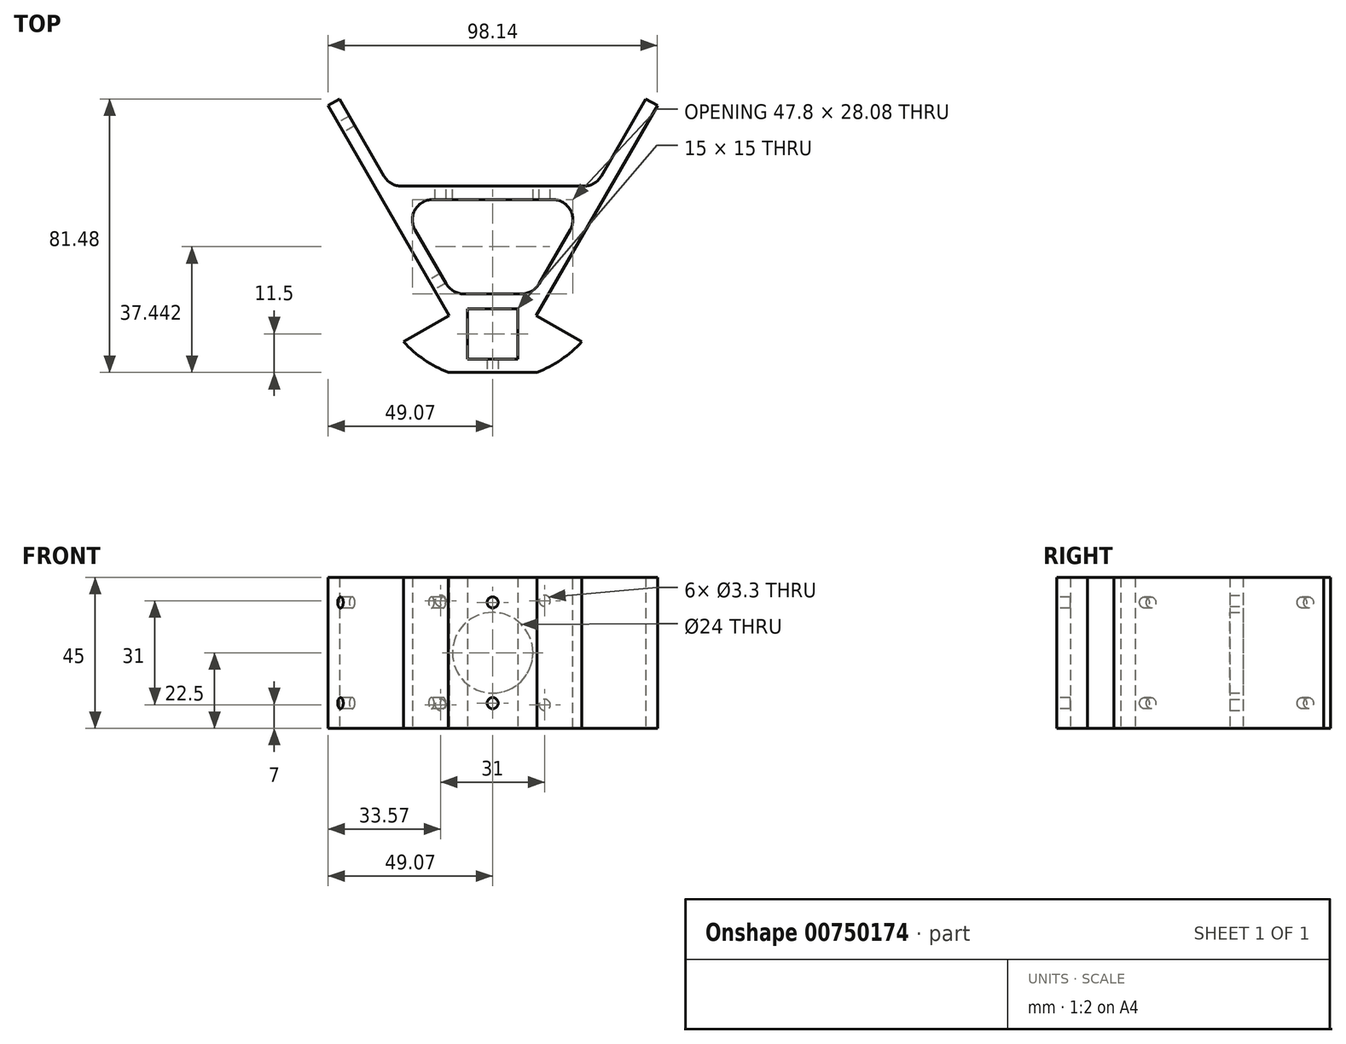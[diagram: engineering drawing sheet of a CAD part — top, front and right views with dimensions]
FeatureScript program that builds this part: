
annotation { "Feature Type Name" : "Feature", "Feature Type Description" : "" }
export const myFeature = defineFeature(function(context is Context, id is Id, definition is map)
    precondition{}
    {
        {
            var Q0;
            Q0=qCreatedBy(makeId("Top.planeOp"),FACE);
            var sketch = newSketch(context, id + "F0", { "sketchPlane" : qUnion([Q0])});
            skLineSegment(sketch, "E0.bottom", {"start": v(7.5, 7.5) * mm, "end": v(-7.5, 7.5) * mm});
            skLineSegment(sketch, "E0.top", {"start": v(7.5, -7.5) * mm, "end": v(-7.5, -7.5) * mm});
            skLineSegment(sketch, "E0.left", {"start": v(7.5, 7.5) * mm, "end": v(7.5, -7.5) * mm});
            skLineSegment(sketch, "E0.right", {"start": v(-7.5, 7.5) * mm, "end": v(-7.5, -7.5) * mm});
            skPoint(sketch, "E0.middle", {"position": v(0, 0) * mm});
            skLineSegment(sketch, "E1", {"start": v(-9.53, 7.48) * mm, "end": v(-12.08, 11.9) * mm, "construction": true});
            skLineSegment(sketch, "E2", {"start": v(-45.61, 69.98) * mm, "end": v(-49.07, 67.98) * mm});
            skLineSegment(sketch, "E3", {"start": v(-49.07, 67.98) * mm, "end": v(-13, 5.48) * mm});
            skPoint(sketch, "E4", {"position": v(0, -14.02) * mm});
            skLineSegment(sketch, "E5", {"start": v(0, -14.02) * mm, "end": v(0, 69.98) * mm, "construction": true});
            skLineSegment(sketch, "E6", {"start": v(-13, 5.48) * mm, "end": v(-26.54, -2.34) * mm});
            skLineSegment(sketch, "E7", {"start": v(-9.53, 7.48) * mm, "end": v(0, 12.98) * mm, "construction": true});
            skLineSegment(sketch, "E8", {"start": v(-13, 5.48) * mm, "end": v(-9.53, 7.48) * mm, "construction": true});
            skLineSegment(sketch, "E9", {"start": v(-8, 8.37) * mm, "end": v(-7.5, 7.5) * mm, "construction": true});
            skLineSegment(sketch, "E10", {"start": v(0, 39.98) * mm, "end": v(-28.3, 39.98) * mm});
            skArc(sketch, "E11.trimOffspring", {"start": v(-26.54, -2.34) * mm, "mid": v(-14.5, -10.97) * mm, "end": v(0, -14.02) * mm});
            skLineSegment(sketch, "E12", {"start": v(0, 43.98) * mm, "end": v(-30.6, 43.98) * mm});
            skLineSegment(sketch, "E13", {"start": v(-12.08, 11.9) * mm, "end": v(-45.61, 69.98) * mm});
            skLineSegment(sketch, "E14.MirrorCS", {"start": v(12.08, 11.9) * mm, "end": v(45.61, 69.98) * mm});
            skLineSegment(sketch, "E15.MirrorCS", {"start": v(45.61, 69.98) * mm, "end": v(49.07, 67.98) * mm});
            skLineSegment(sketch, "E16.MirrorCS", {"start": v(49.07, 67.98) * mm, "end": v(13, 5.48) * mm});
            skLineSegment(sketch, "E17.MirrorCS", {"start": v(13, 5.48) * mm, "end": v(26.54, -2.34) * mm});
            skArc(sketch, "E18.MirrorCS", {"start": v(26.54, -2.34) * mm, "mid": v(14.5, -10.97) * mm, "end": v(0, -14.02) * mm});
            skLineSegment(sketch, "E19.MirrorCS", {"start": v(0, 43.98) * mm, "end": v(30.6, 43.98) * mm});
            skLineSegment(sketch, "E20.MirrorCS", {"start": v(0, 39.98) * mm, "end": v(28.3, 39.98) * mm});
            skLineSegment(sketch, "E21", {"start": v(-12.08, 11.9) * mm, "end": v(0, 11.9) * mm});
            skLineSegment(sketch, "E22.MirrorCS", {"start": v(12.08, 11.9) * mm, "end": v(0, 11.9) * mm});
            skSolve(sketch);
        }
        {
            var Q0;
            Q0=makeQuery(id+"F0.imprint","IMPRINT",FACE,{"disambiguationData":[TD([[makeQuery(id+"F0.imprint","IMPRINT",EDGE,{"derivedFrom":sQuery(id+"F0.wireOp",EDGE,"E0.bottom")}),-1.0]])]});
            var Q1;
            {var subQ1=sQuery(id+"F0.wireOp",EDGE,"E10");Q1=makeQuery(id+"F0.imprint","IMPRINT",FACE,{"disambiguationData":[TD([[makeQuery(id+"F0.imprint","IMPRINT",EDGE,{"derivedFrom":subQ1}),-1.0]])]});}
            extrude(context, id + "F1", {"entities" : qUnion([Q0, Q1]), "depth" : 45 * mm, "offsetDistance" : 25 * mm, "symmetric" : true});
        }
        {
            var Q0;
            Q0=makeQuery(id+"F1.opExtrude","SWEPT_FACE",FACE,{"disambiguationData":[OSD([sQuery(id+"F0.wireOp",EDGE,"E12"),sQuery(id+"F0.wireOp",EDGE,"E19.MirrorCS")])]});
            var sketch = newSketch(context, id + "F2", { "sketchPlane" : qUnion([Q0])});
            skPoint(sketch, "E23", {"position": v(0, 0) * mm});
            skLineSegment(sketch, "E24", {"start": v(15.5, -22.5) * mm, "end": v(15.5, 22.5) * mm, "construction": true});
            skLineSegment(sketch, "E25", {"start": v(-15.5, -22.5) * mm, "end": v(-15.5, 22.5) * mm, "construction": true});
            skPoint(sketch, "E26", {"position": v(15.5, -15.5) * mm});
            skPoint(sketch, "E27", {"position": v(-15.5, -15.5) * mm});
            skPoint(sketch, "E28", {"position": v(15.5, 15.5) * mm});
            skPoint(sketch, "E29", {"position": v(-15.5, 15.5) * mm});
            skCircle(sketch, "E30", {"center": v(0, 0) * mm, "radius": 12 * mm});
            skSolve(sketch);
        }
        {
            var Q0;
            Q0=makeQuery(id+"F2.imprint","IMPRINT",FACE,{"disambiguationData":[TD([[makeQuery(id+"F2.imprint","IMPRINT",EDGE,{"derivedFrom":sQuery(id+"F2.wireOp",EDGE,"E30")}),1.0]])]});
            extrude(context, id + "F3", {"entities" : qUnion([Q0]), "operationType" : NewBodyOperationType.REMOVE, "endBound" : BoundingType.UP_TO_NEXT, "oppositeDirection" : true, "depth" : 25 * mm, "offsetDistance" : 25 * mm});
        }
        {
            var Q0;
            Q0=sQuery(id+"F2.wireOp",VERTEX,"E28");
            var Q1;
            Q1=sQuery(id+"F2.wireOp",VERTEX,"E26");
            var Q2;
            Q2=sQuery(id+"F2.wireOp",VERTEX,"E27");
            var Q3;
            Q3=sQuery(id+"F2.wireOp",VERTEX,"E29");
            var Q4;
            Q4=makeQuery(id+"F1.opExtrude","SWEPT_BODY",BODY,{"disambiguationData":[OSD([sQuery(id+"F0.wireOp",EDGE,"E0.bottom"),sQuery(id+"F0.wireOp",EDGE,"E0.top"),sQuery(id+"F0.wireOp",EDGE,"E0.left"),sQuery(id+"F0.wireOp",EDGE,"E0.right"),sQuery(id+"F0.wireOp",EDGE,"E2"),sQuery(id+"F0.wireOp",EDGE,"E3"),sQuery(id+"F0.wireOp",EDGE,"E6"),sQuery(id+"F0.wireOp",EDGE,"E10"),sQuery(id+"F0.wireOp",EDGE,"E11.trimOffspring"),sQuery(id+"F0.wireOp",EDGE,"E12"),sQuery(id+"F0.wireOp",EDGE,"E13"),sQuery(id+"F0.wireOp",EDGE,"E14.MirrorCS"),sQuery(id+"F0.wireOp",EDGE,"E15.MirrorCS"),sQuery(id+"F0.wireOp",EDGE,"E16.MirrorCS"),sQuery(id+"F0.wireOp",EDGE,"E17.MirrorCS"),sQuery(id+"F0.wireOp",EDGE,"E18.MirrorCS"),sQuery(id+"F0.wireOp",EDGE,"E19.MirrorCS"),sQuery(id+"F0.wireOp",EDGE,"E20.MirrorCS"),sQuery(id+"F0.wireOp",EDGE,"E21"),sQuery(id+"F0.wireOp",EDGE,"E22.MirrorCS")])]});
            hole(context, id + "F4", {"style" : HoleStyle.SIMPLE, "endStyle" : HoleEndStyle.BLIND, "standardTappedOrClearance" : lookupTablePath({ "standard" : "ISO", "fit" : "Normal", "size" : "M3", "type" : "Clearance" }), "standardBlindInLast" : lookupTablePath({ "fit" : "Standard", "standard" : "ISO", "size" : "M3", "type" : "Clearance" }), "holeDiameter" : 3.3 * mm, "majorDiameter" : 3 * mm, "holeDepth" : 4 * mm, "isTappedThrough" : true, "tappedDepth" : 2.1 * mm, "tapClearance" : 3, "locations" : qUnion([Q0, Q1, Q2, Q3]), "scope" : qUnion([Q4])});
        }
        {
            var Q0;
            Q0=makeQuery(id+"F1.opExtrude","SWEPT_FACE",FACE,{"disambiguationData":[OSD([sQuery(id+"F0.wireOp",EDGE,"E3")])]});
            var sketch = newSketch(context, id + "F5", { "sketchPlane" : qUnion([Q0])});
            skPoint(sketch, "E31", {"position": v(-21.75, -15) * mm});
            skPoint(sketch, "E32", {"position": v(-75.91, -15) * mm});
            skLineSegment(sketch, "E33", {"start": v(0, 0) * mm, "end": v(-83.41, 0) * mm, "construction": true});
            skPoint(sketch, "E34.MirrorP", {"position": v(-21.75, 15) * mm});
            skPoint(sketch, "E35.MirrorP", {"position": v(-75.91, 15) * mm});
            skSolve(sketch);
        }
        {
            var Q0;
            Q0=sQuery(id+"F5.wireOp",VERTEX,"E31");
            var Q1;
            Q1=sQuery(id+"F5.wireOp",VERTEX,"E32");
            var Q2;
            Q2=sQuery(id+"F5.wireOp",VERTEX,"E35.MirrorP");
            var Q3;
            Q3=sQuery(id+"F5.wireOp",VERTEX,"E34.MirrorP");
            var Q4;
            Q4=makeQuery(id+"F1.opExtrude","SWEPT_BODY",BODY,{"disambiguationData":[OSD([sQuery(id+"F0.wireOp",EDGE,"E0.bottom"),sQuery(id+"F0.wireOp",EDGE,"E0.top"),sQuery(id+"F0.wireOp",EDGE,"E0.left"),sQuery(id+"F0.wireOp",EDGE,"E0.right"),sQuery(id+"F0.wireOp",EDGE,"E2"),sQuery(id+"F0.wireOp",EDGE,"E3"),sQuery(id+"F0.wireOp",EDGE,"E6"),sQuery(id+"F0.wireOp",EDGE,"E10"),sQuery(id+"F0.wireOp",EDGE,"E11.trimOffspring"),sQuery(id+"F0.wireOp",EDGE,"E12"),sQuery(id+"F0.wireOp",EDGE,"E13"),sQuery(id+"F0.wireOp",EDGE,"E14.MirrorCS"),sQuery(id+"F0.wireOp",EDGE,"E15.MirrorCS"),sQuery(id+"F0.wireOp",EDGE,"E16.MirrorCS"),sQuery(id+"F0.wireOp",EDGE,"E17.MirrorCS"),sQuery(id+"F0.wireOp",EDGE,"E18.MirrorCS"),sQuery(id+"F0.wireOp",EDGE,"E19.MirrorCS"),sQuery(id+"F0.wireOp",EDGE,"E20.MirrorCS"),sQuery(id+"F0.wireOp",EDGE,"E21"),sQuery(id+"F0.wireOp",EDGE,"E22.MirrorCS")])]});
            hole(context, id + "F6", {"style" : HoleStyle.SIMPLE, "endStyle" : HoleEndStyle.BLIND, "standardTappedOrClearance" : lookupTablePath({ "standard" : "ISO", "fit" : "Normal", "size" : "M3", "type" : "Clearance" }), "standardBlindInLast" : lookupTablePath({ "fit" : "Standard", "standard" : "ISO", "size" : "M3", "type" : "Clearance" }), "holeDiameter" : 3.3 * mm, "majorDiameter" : 5 * mm, "holeDepth" : 4 * mm, "isTappedThrough" : true, "tappedDepth" : 2.1 * mm, "tapClearance" : 3, "locations" : qUnion([Q0, Q1, Q2, Q3]), "scope" : qUnion([Q4])});
        }
        {
            var Q0;
            Q0=makeQuery(id+"F1.opExtrude","SWEPT_EDGE",EDGE,{"disambiguationData":[OSD([sQuery(id+"F0.wireOp",EDGE,"E10"),sQuery(id+"F0.wireOp",EDGE,"E13")])]});
            var Q1;
            Q1=makeQuery(id+"F1.opExtrude","SWEPT_EDGE",EDGE,{"disambiguationData":[OSD([sQuery(id+"F0.wireOp",EDGE,"E13"),sQuery(id+"F0.wireOp",EDGE,"E21")])]});
            var Q2;
            Q2=makeQuery(id+"F1.opExtrude","SWEPT_EDGE",EDGE,{"disambiguationData":[OSD([sQuery(id+"F0.wireOp",EDGE,"E14.MirrorCS"),sQuery(id+"F0.wireOp",EDGE,"E22.MirrorCS")])]});
            var Q3;
            Q3=makeQuery(id+"F1.opExtrude","SWEPT_EDGE",EDGE,{"disambiguationData":[OSD([sQuery(id+"F0.wireOp",EDGE,"E14.MirrorCS"),sQuery(id+"F0.wireOp",EDGE,"E20.MirrorCS")])]});
            var Q4;
            Q4=makeQuery(id+"F1.opExtrude","SWEPT_EDGE",EDGE,{"disambiguationData":[OSD([sQuery(id+"F0.wireOp",EDGE,"E12"),sQuery(id+"F0.wireOp",EDGE,"E13")])]});
            var Q5;
            Q5=makeQuery(id+"F1.opExtrude","SWEPT_EDGE",EDGE,{"disambiguationData":[OSD([sQuery(id+"F0.wireOp",EDGE,"E14.MirrorCS"),sQuery(id+"F0.wireOp",EDGE,"E19.MirrorCS")])]});
            fillet(context, id + "F7", {"entities" : qUnion([Q0, Q1, Q2, Q3, Q4, Q5]), "radius" : 6 * mm, "tangentPropagation" : true, "allowEdgeOverflow" : false});
        }
        {
            var Q0;
            Q0=makeQuery(id+"F1.opExtrude","CAP_FACE",FACE,{"disambiguationData":[OSD([sQuery(id+"F0.wireOp",EDGE,"E0.bottom"),sQuery(id+"F0.wireOp",EDGE,"E0.top"),sQuery(id+"F0.wireOp",EDGE,"E0.left"),sQuery(id+"F0.wireOp",EDGE,"E0.right"),sQuery(id+"F0.wireOp",EDGE,"E2"),sQuery(id+"F0.wireOp",EDGE,"E3"),sQuery(id+"F0.wireOp",EDGE,"E6"),sQuery(id+"F0.wireOp",EDGE,"E10"),sQuery(id+"F0.wireOp",EDGE,"E11.trimOffspring"),sQuery(id+"F0.wireOp",EDGE,"E12"),sQuery(id+"F0.wireOp",EDGE,"E13"),sQuery(id+"F0.wireOp",EDGE,"E14.MirrorCS"),sQuery(id+"F0.wireOp",EDGE,"E15.MirrorCS"),sQuery(id+"F0.wireOp",EDGE,"E16.MirrorCS"),sQuery(id+"F0.wireOp",EDGE,"E17.MirrorCS"),sQuery(id+"F0.wireOp",EDGE,"E18.MirrorCS"),sQuery(id+"F0.wireOp",EDGE,"E19.MirrorCS"),sQuery(id+"F0.wireOp",EDGE,"E20.MirrorCS"),sQuery(id+"F0.wireOp",EDGE,"E21"),sQuery(id+"F0.wireOp",EDGE,"E22.MirrorCS")])],"isStart":false});
            var sketch = newSketch(context, id + "F8", { "sketchPlane" : qUnion([Q0])});
            skLineSegment(sketch, "E36", {"start": v(-13.22, -11.5) * mm, "end": v(13.22, -11.5) * mm});
            skSolve(sketch);
        }
        {
            var Q0;
            {var subQ0=sQuery(id+"F8.wireOp",EDGE,"E36");Q0=makeQuery(id+"F8.imprint","IMPRINT",FACE,{"disambiguationData":[TD([[makeQuery(id+"F8.imprint","IMPRINT",EDGE,{"derivedFrom":subQ0}),-1.0]])]});}
            extrude(context, id + "F9", {"entities" : qUnion([Q0]), "operationType" : NewBodyOperationType.REMOVE, "endBound" : BoundingType.UP_TO_NEXT, "oppositeDirection" : true, "depth" : 25 * mm, "offsetDistance" : 25 * mm});
        }
        {
            var Q0;
            Q0=makeQuery(id+"F9.boolean.opBoolean","COPY",FACE,{"derivedFrom":makeQuery(id+"F9.opExtrude","SWEPT_FACE",FACE,{"disambiguationData":[OSD([sQuery(id+"F8.wireOp",EDGE,"E36")])]})});
            var sketch = newSketch(context, id + "F10", { "sketchPlane" : qUnion([Q0])});
            skPoint(sketch, "E37", {"position": v(0, 15) * mm});
            skPoint(sketch, "E38", {"position": v(0, -15) * mm});
            skEllipse(sketch, "E39.0", {"center": v(-45.32, -15) * mm, "majorRadius": 1.65 * mm, "minorRadius": 0.83 * mm, "majorAxis": v(0, 1)});
            skEllipse(sketch, "E40.0", {"center": v(-45.32, 15) * mm, "majorRadius": 1.65 * mm, "minorRadius": 0.83 * mm, "majorAxis": v(0, 1)});
            skSolve(sketch);
        }
        {
            var Q0;
            Q0=sQuery(id+"F10.wireOp",VERTEX,"E37");
            var Q1;
            Q1=sQuery(id+"F10.wireOp",VERTEX,"E38");
            var Q2;
            Q2=makeQuery(id+"F1.opExtrude","SWEPT_BODY",BODY,{"disambiguationData":[OSD([sQuery(id+"F0.wireOp",EDGE,"E0.bottom"),sQuery(id+"F0.wireOp",EDGE,"E0.top"),sQuery(id+"F0.wireOp",EDGE,"E0.left"),sQuery(id+"F0.wireOp",EDGE,"E0.right"),sQuery(id+"F0.wireOp",EDGE,"E2"),sQuery(id+"F0.wireOp",EDGE,"E3"),sQuery(id+"F0.wireOp",EDGE,"E6"),sQuery(id+"F0.wireOp",EDGE,"E10"),sQuery(id+"F0.wireOp",EDGE,"E11.trimOffspring"),sQuery(id+"F0.wireOp",EDGE,"E12"),sQuery(id+"F0.wireOp",EDGE,"E13"),sQuery(id+"F0.wireOp",EDGE,"E14.MirrorCS"),sQuery(id+"F0.wireOp",EDGE,"E15.MirrorCS"),sQuery(id+"F0.wireOp",EDGE,"E16.MirrorCS"),sQuery(id+"F0.wireOp",EDGE,"E17.MirrorCS"),sQuery(id+"F0.wireOp",EDGE,"E18.MirrorCS"),sQuery(id+"F0.wireOp",EDGE,"E19.MirrorCS"),sQuery(id+"F0.wireOp",EDGE,"E20.MirrorCS"),sQuery(id+"F0.wireOp",EDGE,"E21"),sQuery(id+"F0.wireOp",EDGE,"E22.MirrorCS")])]});
            hole(context, id + "F11", {"style" : HoleStyle.SIMPLE, "endStyle" : HoleEndStyle.BLIND, "standardTappedOrClearance" : lookupTablePath({ "standard" : "ISO", "fit" : "Normal", "size" : "M3", "type" : "Clearance" }), "standardBlindInLast" : lookupTablePath({ "fit" : "Standard", "standard" : "ISO", "size" : "M3", "type" : "Clearance" }), "holeDiameter" : 3.3 * mm, "majorDiameter" : 5 * mm, "holeDepth" : 4 * mm, "isTappedThrough" : true, "tappedDepth" : 35.62 * mm, "tapClearance" : 3, "locations" : qUnion([Q0, Q1]), "scope" : qUnion([Q2])});
        }
        {
            var Q0;
            Q0=makeQuery(id+"F1.opExtrude","SWEPT_FACE",FACE,{"disambiguationData":[OSD([sQuery(id+"F0.wireOp",EDGE,"E17.MirrorCS")])]});
            var sketch = newSketch(context, id + "F12", { "sketchPlane" : qUnion([Q0])});
            skLineSegment(sketch, "E41.0", {"start": v(-8.5, -16.65) * mm, "end": v(-8.5, -13.35) * mm});
            skLineSegment(sketch, "E42.0", {"start": v(-8.5, 13.35) * mm, "end": v(-8.5, 16.65) * mm});
            skLineSegment(sketch, "E43", {"start": v(-8.5, 15) * mm, "end": v(-24.15, 15) * mm});
            skLineSegment(sketch, "E44", {"start": v(-8.5, -15) * mm, "end": v(-24.15, -15) * mm});
            skPoint(sketch, "E45", {"position": v(-16.33, 15) * mm});
            skPoint(sketch, "E46", {"position": v(-16.33, -15) * mm});
            skSolve(sketch);
        }
        {
            var Q0;
            Q0=makeQuery(id+"F1.opExtrude","SWEPT_FACE",FACE,{"disambiguationData":[OSD([sQuery(id+"F0.wireOp",EDGE,"E6")])]});
            var sketch = newSketch(context, id + "F13", { "sketchPlane" : qUnion([Q0])});
            skLineSegment(sketch, "E47.0", {"start": v(8.5, 16.65) * mm, "end": v(8.5, 13.35) * mm});
            skLineSegment(sketch, "E47.1", {"start": v(8.5, -13.35) * mm, "end": v(8.5, -16.65) * mm});
            skLineSegment(sketch, "E48", {"start": v(8.5, 15) * mm, "end": v(24.15, 15) * mm});
            skLineSegment(sketch, "E49", {"start": v(8.5, -15) * mm, "end": v(24.15, -15) * mm});
            skSolve(sketch);
        }
        {
            var Q0;
            Q0=makeQuery(id+"F1.opExtrude","CAP_FACE",FACE,{"disambiguationData":[OSD([sQuery(id+"F0.wireOp",EDGE,"E0.bottom"),sQuery(id+"F0.wireOp",EDGE,"E0.top"),sQuery(id+"F0.wireOp",EDGE,"E0.left"),sQuery(id+"F0.wireOp",EDGE,"E0.right"),sQuery(id+"F0.wireOp",EDGE,"E2"),sQuery(id+"F0.wireOp",EDGE,"E3"),sQuery(id+"F0.wireOp",EDGE,"E6"),sQuery(id+"F0.wireOp",EDGE,"E10"),sQuery(id+"F0.wireOp",EDGE,"E11.trimOffspring"),sQuery(id+"F0.wireOp",EDGE,"E12"),sQuery(id+"F0.wireOp",EDGE,"E13"),sQuery(id+"F0.wireOp",EDGE,"E14.MirrorCS"),sQuery(id+"F0.wireOp",EDGE,"E15.MirrorCS"),sQuery(id+"F0.wireOp",EDGE,"E16.MirrorCS"),sQuery(id+"F0.wireOp",EDGE,"E17.MirrorCS"),sQuery(id+"F0.wireOp",EDGE,"E18.MirrorCS"),sQuery(id+"F0.wireOp",EDGE,"E19.MirrorCS"),sQuery(id+"F0.wireOp",EDGE,"E20.MirrorCS"),sQuery(id+"F0.wireOp",EDGE,"E21"),sQuery(id+"F0.wireOp",EDGE,"E22.MirrorCS")])],"isStart":true});
            var sketch = newSketch(context, id + "F14", { "sketchPlane" : qUnion([Q0])});
            skLineSegment(sketch, "E50", {"start": v(7.5, -7.5) * mm, "end": v(-7.5, 7.5) * mm});
            skLineSegment(sketch, "E51", {"start": v(-7.5, -7.5) * mm, "end": v(7.5, 7.5) * mm});
            skPoint(sketch, "E52", {"position": v(0, 0) * mm});
            skSolve(sketch);
        }
    });
